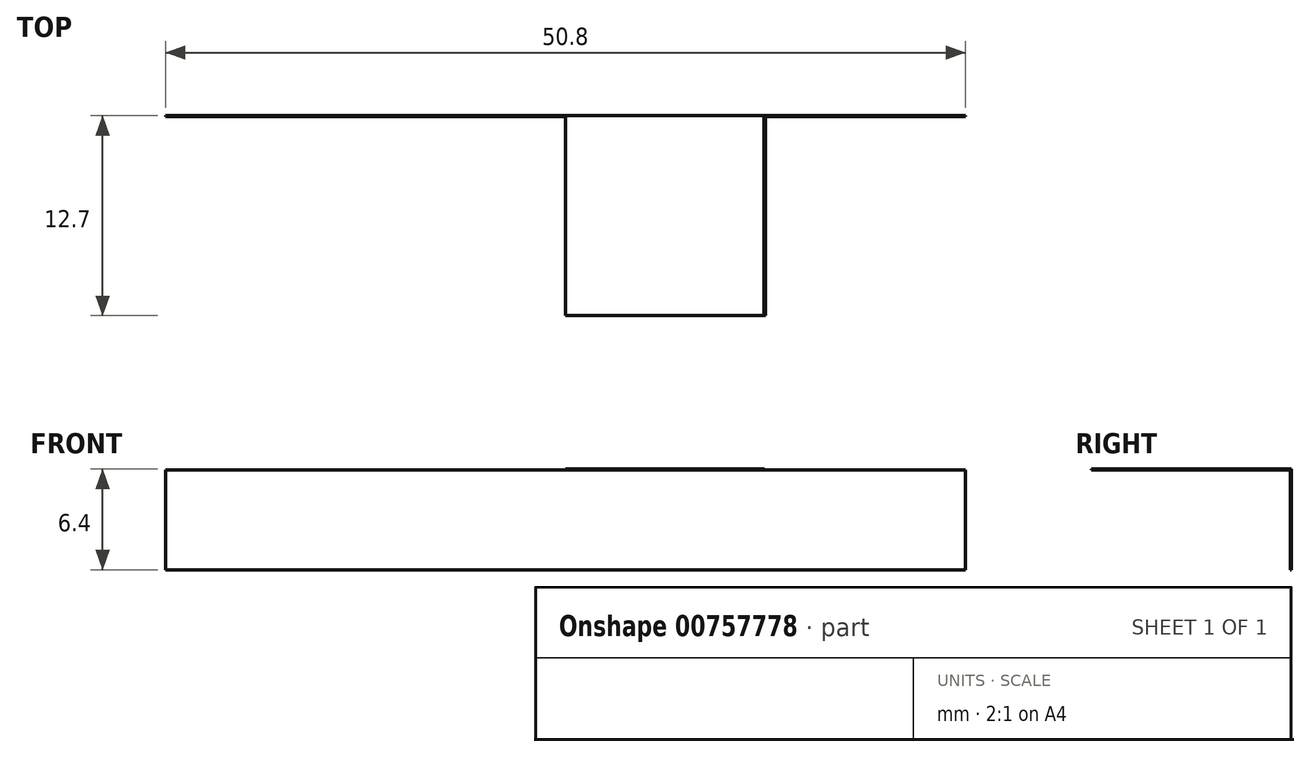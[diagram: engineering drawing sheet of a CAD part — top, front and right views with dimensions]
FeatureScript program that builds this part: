
annotation { "Feature Type Name" : "Feature", "Feature Type Description" : "" }
export const myFeature = defineFeature(function(context is Context, id is Id, definition is map)
    precondition{}
    {
        {
            var Q0;
            Q0=qCreatedBy(makeId("Front.planeOp"),FACE);
            var sketch = newSketch(context, id + "F0", { "sketchPlane" : qUnion([Q0])});
            skLineSegment(sketch, "E0", {"start": v(-34.74, 0) * mm, "end": v(28.76, 0) * mm});
            skLineSegment(sketch, "E1", {"start": v(28.76, 0) * mm, "end": v(28.76, 6.35) * mm});
            skLineSegment(sketch, "E2", {"start": v(28.76, 6.35) * mm, "end": v(-34.74, 6.35) * mm});
            skLineSegment(sketch, "E3", {"start": v(-34.74, 6.35) * mm, "end": v(-34.74, 0) * mm});
            skSolve(sketch);
        }
        {
            var Q0;
            Q0 = qSketchRegion(id + "F0", true);
            extrude(context, id + "F1", {"entities" : qUnion([Q0]), "depth" : 6 / 101.6 * mm, "offsetDistance" : 25.4 * mm});
        }
        {
            var Q0;
            Q0=makeQuery(id+"F1.opExtrude","SWEPT_FACE",FACE,{"disambiguationData":[OSD([sQuery(id+"F0.wireOp",EDGE,"E2")])]});
            var sketch = newSketch(context, id + "F2", { "sketchPlane" : qUnion([Q0])});
            skLineSegment(sketch, "E4", {"start": v(3.36, 0) * mm, "end": v(3.36, -12.7) * mm});
            skLineSegment(sketch, "E5", {"start": v(3.36, -12.7) * mm, "end": v(-34.74, -12.7) * mm});
            skLineSegment(sketch, "E6", {"start": v(-34.74, -12.7) * mm, "end": v(-34.74, 0) * mm});
            skLineSegment(sketch, "E7", {"start": v(-34.74, 0) * mm, "end": v(3.36, 0) * mm});
            skSolve(sketch);
        }
        {
            var Q0;
            Q0 = qSketchRegion(id + "F2", true);
            extrude(context, id + "F3", {"entities" : qUnion([Q0]), "operationType" : NewBodyOperationType.ADD, "depth" : 5 / 101.6 * mm, "offsetDistance" : 25.4 * mm});
        }
        {
            var Q0;
            Q0=makeQuery(id+"F3.opExtrude","SWEPT_FACE",FACE,{"disambiguationData":[OSD([sQuery(id+"F2.wireOp",EDGE,"E5")])]});
            var sketch = newSketch(context, id + "F4", { "sketchPlane" : qUnion([Q0])});
            skLineSegment(sketch, "E8", {"start": v(-9.34, 38.1) * mm, "end": v(-9.34, 6.35) * mm});
            skLineSegment(sketch, "E9", {"start": v(-34.74, 25.4) * mm, "end": v(-9.34, 25.4) * mm});
            skCircle(sketch, "E10", {"center": v(-22.04, 25.4) * mm, "radius": 6.35 * mm});
            skArc(sketch, "E11", {"start": v(-9.34, 25.4) * mm, "mid": v(-22.04, 38.12) * mm, "end": v(-34.74, 25.4) * mm});
            skArc(sketch, "E12", {"start": v(-9.34, 25.4) * mm, "mid": v(-5.77, 14.02) * mm, "end": v(3.36, 6.35) * mm});
            skSolve(sketch);
        }
        {
            var Q0;
            {var subQ0=sQuery(id+"F4.wireOp",EDGE,"E10");var subQ1=sQuery(id+"F4.wireOp",EDGE,"E9");var subQ2=makeQuery(id+"F4.imprint","INTERSECT",VERTEX,{"disambiguationData":[OD(0.0)],"derivedFrom":[subQ1,subQ0]});Q0=makeQuery(id+"F4.imprint","IMPRINT",FACE,{"disambiguationData":[TD([[makeQuery(id+"F4.imprint","IMPRINT",EDGE,{"disambiguationData":[TD([[subQ2,-1.0]])],"derivedFrom":subQ1}),1.0]])]});}
            var Q1;
            {var subQ0=sQuery(id+"F4.wireOp",EDGE,"E10");var subQ1=sQuery(id+"F4.wireOp",EDGE,"E9");var subQ2=makeQuery(id+"F4.imprint","INTERSECT",VERTEX,{"disambiguationData":[OD(0.0)],"derivedFrom":[subQ1,subQ0]});Q1=makeQuery(id+"F4.imprint","IMPRINT",FACE,{"disambiguationData":[TD([[makeQuery(id+"F4.imprint","IMPRINT",EDGE,{"disambiguationData":[TD([[subQ2,-1.0]])],"derivedFrom":subQ1}),-1.0]])]});}
            var Q2;
            {var subQ0=sQuery(id+"F4.wireOp",EDGE,"E11");var subQ1=makeQuery(id+"F3.opExtrude","CAP_EDGE",EDGE,{"disambiguationData":[OSD([sQuery(id+"F2.wireOp",EDGE,"E5")])],"isStart":false});var subQ2=makeQuery(id+"F4.imprint","INTERSECT",VERTEX,{"disambiguationData":[OD(0.0)],"derivedFrom":[subQ1,subQ0]});Q2=makeQuery(id+"F4.imprint","IMPRINT",FACE,{"disambiguationData":[TD([[makeQuery(id+"F4.imprint","IMPRINT",EDGE,{"disambiguationData":[TD([[subQ2,-1.0]])],"derivedFrom":subQ0}),1.0]])]});}
            var Q3;
            {var subQ0=sQuery(id+"F4.wireOp",EDGE,"E11");var subQ1=sQuery(id+"F2.wireOp",EDGE,"E5");var subQ4=makeQuery(id+"F3.opExtrude","CAP_EDGE",EDGE,{"disambiguationData":[OSD([subQ1])],"isStart":false});var subQ5=makeQuery(id+"F4.imprint","INTERSECT",VERTEX,{"disambiguationData":[OD(1.0)],"derivedFrom":[subQ4,subQ0]});Q3=makeQuery(id+"F4.imprint","IMPRINT",FACE,{"disambiguationData":[TD([[makeQuery(id+"F4.imprint","IMPRINT",EDGE,{"disambiguationData":[TD([[subQ5,-1.0]])],"derivedFrom":subQ0}),-1.0]])]});}
            var Q4;
            {var subQ0=sQuery(id+"F4.wireOp",EDGE,"E8");var subQ1=makeQuery(id+"F3.opExtrude","CAP_EDGE",EDGE,{"disambiguationData":[OSD([sQuery(id+"F2.wireOp",EDGE,"E5")])],"isStart":false});var subQ2=makeQuery(id+"F4.imprint","INTERSECT",VERTEX,{"derivedFrom":[subQ1,subQ0]});Q4=makeQuery(id+"F4.imprint","IMPRINT",FACE,{"disambiguationData":[TD([[makeQuery(id+"F4.imprint","IMPRINT",EDGE,{"disambiguationData":[TD([[subQ2,-1.0]])],"derivedFrom":subQ0}),-1.0]])]});}
            var Q5;
            {var subQ2=sQuery(id+"F4.wireOp",EDGE,"E12");Q5=makeQuery(id+"F4.imprint","IMPRINT",FACE,{"disambiguationData":[TD([[makeQuery(id+"F4.imprint","IMPRINT",EDGE,{"derivedFrom":subQ2}),1.0]])]});}
            extrude(context, id + "F5", {"entities" : qUnion([Q0, Q1, Q2, Q3, Q4, Q5]), "operationType" : NewBodyOperationType.REMOVE, "endBound" : BoundingType.THROUGH_ALL, "oppositeDirection" : true, "depth" : 25.4 * mm, "offsetDistance" : 25.4 * mm});
        }
        {
            var Q0;
            Q0=makeQuery(id+"F1.opExtrude","SWEPT_FACE",FACE,{"disambiguationData":[OSD([sQuery(id+"F0.wireOp",EDGE,"E2")])]});
            var sketch = newSketch(context, id + "F6", { "sketchPlane" : qUnion([Q0])});
            skLineSegment(sketch, "E13", {"start": v(-22.04, -12.7) * mm, "end": v(-22.04, -38.1) * mm});
            skLineSegment(sketch, "E14", {"start": v(16.06, 0) * mm, "end": v(16.06, -38.1) * mm});
            skLineSegment(sketch, "E15", {"start": v(-34.74, -31.75) * mm, "end": v(28.76, -31.75) * mm});
            skLineSegment(sketch, "E16", {"start": v(-34.74, -25.4) * mm, "end": v(28.76, -25.4) * mm});
            skLineSegment(sketch, "E17", {"start": v(-28.39, -12.7) * mm, "end": v(-28.39, -38.1) * mm});
            skLineSegment(sketch, "E18", {"start": v(22.41, 0) * mm, "end": v(22.41, -38.1) * mm});
            skCircle(sketch, "E19", {"center": v(-25.23, -28.65) * mm, "radius": 3.02 * mm});
            skCircle(sketch, "E20", {"center": v(19.2, -28.65) * mm, "radius": 3.14 * mm});
            skLineSegment(sketch, "E21", {"start": v(3.36, -6.35) * mm, "end": v(28.76, -6.35) * mm});
            skLineSegment(sketch, "E22", {"start": v(3.36, -12.7) * mm, "end": v(28.76, -12.7) * mm});
            skCircle(sketch, "E23", {"center": v(19.2, -9.55) * mm, "radius": 3.14 * mm});
            skArc(sketch, "E24", {"start": v(-34.74, -25.4) * mm, "mid": v(-31.17, -34.53) * mm, "end": v(-22.04, -38.1) * mm});
            skArc(sketch, "E25", {"start": v(16.06, -38.1) * mm, "mid": v(25.4, -34.74) * mm, "end": v(28.76, -25.4) * mm});
            skSolve(sketch);
        }
        {
            var Q0;
            Q0=makeQuery(id+"F6.imprint","IMPRINT",FACE,{"disambiguationData":[TD([[makeQuery(id+"F6.imprint","IMPRINT",EDGE,{"derivedFrom":sQuery(id+"F6.wireOp",EDGE,"E23")}),1.0]])]});
            var Q1;
            {var subQ0=sQuery(id+"F6.wireOp",EDGE,"E20");var subQ1=sQuery(id+"F6.wireOp",EDGE,"E15");var subQ2=makeQuery(id+"F6.imprint","INTERSECT",VERTEX,{"disambiguationData":[OD(0.0)],"derivedFrom":[subQ1,subQ0]});Q1=makeQuery(id+"F6.imprint","IMPRINT",FACE,{"disambiguationData":[TD([[makeQuery(id+"F6.imprint","IMPRINT",EDGE,{"disambiguationData":[TD([[subQ2,-1.0]])],"derivedFrom":subQ1}),-1.0]])]});}
            var Q2;
            Q2=makeQuery(id+"F6.imprint","IMPRINT",FACE,{"disambiguationData":[TD([[makeQuery(id+"F6.imprint","IMPRINT",EDGE,{"derivedFrom":sQuery(id+"F6.wireOp",EDGE,"E19")}),1.0]])]});
            var Q3;
            {var subQ0=sQuery(id+"F6.wireOp",EDGE,"E20");var subQ1=sQuery(id+"F6.wireOp",EDGE,"E15");var subQ2=makeQuery(id+"F6.imprint","INTERSECT",VERTEX,{"disambiguationData":[OD(0.0)],"derivedFrom":[subQ1,subQ0]});Q3=makeQuery(id+"F6.imprint","IMPRINT",FACE,{"disambiguationData":[TD([[makeQuery(id+"F6.imprint","IMPRINT",EDGE,{"disambiguationData":[TD([[subQ2,-1.0]])],"derivedFrom":subQ1}),1.0]])]});}
            var Q4;
            {var subQ0=sQuery(id+"F0.wireOp",EDGE,"E2");var subQ2=makeQuery(id+"F1.opExtrude","CAP_EDGE",EDGE,{"disambiguationData":[OSD([subQ0])],"isStart":false});var subQ4=sQuery(id+"F6.wireOp",EDGE,"E17");var subQ5=makeQuery(id+"F6.imprint","INTERSECT",VERTEX,{"derivedFrom":[subQ2,subQ4]});Q4=makeQuery(id+"F6.imprint","IMPRINT",FACE,{"disambiguationData":[TD([[makeQuery(id+"F6.imprint","IMPRINT",EDGE,{"disambiguationData":[TD([[subQ5,1.0]])],"derivedFrom":subQ4}),-1.0]])]});}
            var Q5;
            {var subQ0=sQuery(id+"F6.wireOp",EDGE,"E15");var subQ3=sQuery(id+"F6.wireOp",EDGE,"E24");var subQ4=makeQuery(id+"F6.imprint","INTERSECT",VERTEX,{"derivedFrom":[subQ0,subQ3]});Q5=makeQuery(id+"F6.imprint","IMPRINT",FACE,{"disambiguationData":[TD([[makeQuery(id+"F6.imprint","IMPRINT",EDGE,{"disambiguationData":[TD([[subQ4,1.0]])],"derivedFrom":subQ0}),1.0]])]});}
            var Q6;
            {var subQ0=sQuery(id+"F6.wireOp",EDGE,"E17");var subQ1=makeQuery(id+"F1.opExtrude","CAP_EDGE",EDGE,{"disambiguationData":[OSD([sQuery(id+"F0.wireOp",EDGE,"E2")])],"isStart":false});var subQ2=makeQuery(id+"F6.imprint","INTERSECT",VERTEX,{"derivedFrom":[subQ1,subQ0]});Q6=makeQuery(id+"F6.imprint","IMPRINT",FACE,{"disambiguationData":[TD([[makeQuery(id+"F6.imprint","IMPRINT",EDGE,{"disambiguationData":[TD([[subQ2,1.0]])],"derivedFrom":subQ0}),1.0]])]});}
            var Q7;
            {var subQ0=sQuery(id+"F0.wireOp",EDGE,"E2");var subQ1=makeQuery(id+"F1.opExtrude","CAP_EDGE",EDGE,{"disambiguationData":[OSD([subQ0])],"isStart":false});var subQ8=sQuery(id+"F6.wireOp",EDGE,"E18");var subQ10=makeQuery(id+"F6.imprint","INTERSECT",VERTEX,{"derivedFrom":[subQ1,subQ8]});Q7=makeQuery(id+"F6.imprint","IMPRINT",FACE,{"disambiguationData":[TD([[makeQuery(id+"F6.imprint","IMPRINT",EDGE,{"disambiguationData":[TD([[subQ10,1.0]])],"derivedFrom":subQ8}),1.0]])]});}
            var Q8;
            {var subQ0=sQuery(id+"F6.wireOp",EDGE,"E18");var subQ1=makeQuery(id+"F1.opExtrude","CAP_EDGE",EDGE,{"disambiguationData":[OSD([sQuery(id+"F0.wireOp",EDGE,"E2")])],"isStart":false});var subQ2=makeQuery(id+"F6.imprint","INTERSECT",VERTEX,{"derivedFrom":[subQ1,subQ0]});Q8=makeQuery(id+"F6.imprint","IMPRINT",FACE,{"disambiguationData":[TD([[makeQuery(id+"F6.imprint","IMPRINT",EDGE,{"disambiguationData":[TD([[subQ2,1.0]])],"derivedFrom":subQ0}),-1.0]])]});}
            var Q9;
            {var subQ0=sQuery(id+"F6.wireOp",EDGE,"E15");var subQ3=sQuery(id+"F6.wireOp",EDGE,"E25");var subQ4=makeQuery(id+"F6.imprint","INTERSECT",VERTEX,{"derivedFrom":[subQ0,subQ3]});Q9=makeQuery(id+"F6.imprint","IMPRINT",FACE,{"disambiguationData":[TD([[makeQuery(id+"F6.imprint","IMPRINT",EDGE,{"disambiguationData":[TD([[subQ4,-1.0]])],"derivedFrom":subQ0}),1.0]])]});}
            extrude(context, id + "F7", {"entities" : qUnion([Q0, Q1, Q2, Q3, Q4, Q5, Q6, Q7, Q8, Q9]), "operationType" : NewBodyOperationType.REMOVE, "endBound" : BoundingType.THROUGH_ALL, "oppositeDirection" : true, "depth" : 25.4 * mm, "offsetDistance" : 25.4 * mm});
        }
    });
